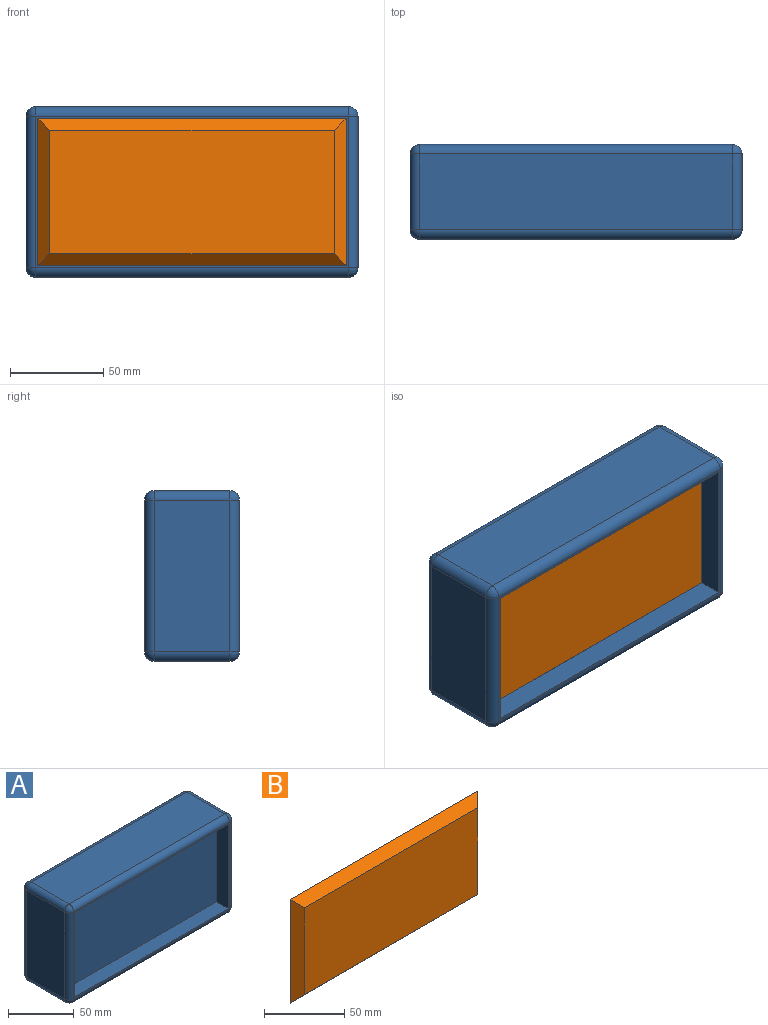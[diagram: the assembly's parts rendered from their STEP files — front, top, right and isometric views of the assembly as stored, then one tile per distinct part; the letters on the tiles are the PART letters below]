
ASSEMBLY  parts=2 mates=1
PART A: 31 faces, bbox 177.8x50.8x91.4 mm
  f0: plane 167.64x81.28mm, normal (0,-1,0), area 625.8mm2, adj f6,f7,f8,f9,f14,f15,f24,f25
  f1: plane 81.28x40.64mm, normal (1,0,0), area 3303.2mm2, adj f19,f24,f27,f30
  f2: plane 167.64x40.64mm, normal (0,0,1), area 6812.9mm2, adj f16,f25,f26,f30
  f3: plane 81.28x40.64mm, normal (-1,0,0), area 3303.2mm2, adj f11,f15,f16,f17
  f4: plane 167.64x40.64mm, normal (0,0,-1), area 6812.9mm2, adj f11,f14,f18,f19
  f5: plane 167.64x81.28mm, normal (0,1,0), area 13625.8mm2, adj f17,f18,f26,f27
  f6: plane 78.74x12.7mm, normal (1,0,0), area 1000mm2, adj f0,f7,f9,f10
  f7: plane 165.1x12.7mm, normal (0,0,1), area 2096.8mm2, adj f0,f6,f8,f10
  f8: plane 78.74x12.7mm, normal (-1,0,0), area 1000mm2, adj f0,f7,f9,f10
  f9: plane 165.1x12.7mm, normal (0,0,-1), area 2096.8mm2, adj f0,f6,f8,f10
  f10: plane 165.1x78.74mm, normal (0,-1,0), area 13000mm2, adj f6,f7,f8,f9
  f11: cylinder r=5.08mm len=40.64mm, axis (0,1,0), area 324.3mm2, adj f3,f4,f12,f13
  f12: sphere r=5.08mm, area 40.5mm2, adj f11,f14,f15
  f13: sphere r=5.08mm, area 40.5mm2, adj f11,f17,f18
  f14: cylinder r=5.08mm len=167.64mm, axis (-1,0,0), area 1337.7mm2, adj f0,f4,f12,f20
  f15: cylinder r=5.08mm len=81.28mm, axis (0,0,1), area 648.6mm2, adj f0,f3,f12,f21
  f16: cylinder r=5.08mm len=40.64mm, axis (0,-1,0), area 324.3mm2, adj f2,f3,f21,f22
  f17: cylinder r=5.08mm len=81.28mm, axis (0,0,-1), area 648.6mm2, adj f3,f5,f13,f22
  f18: cylinder r=5.08mm len=167.64mm, axis (1,0,0), area 1337.7mm2, adj f4,f5,f13,f23
  f19: cylinder r=5.08mm len=40.64mm, axis (0,-1,0), area 324.3mm2, adj f1,f4,f20,f23
  f20: sphere r=5.08mm, area 40.5mm2, adj f14,f19,f24
  f21: sphere r=5.08mm, area 40.5mm2, adj f15,f16,f25
  f22: sphere r=5.08mm, area 40.5mm2, adj f16,f17,f26
  f23: sphere r=5.08mm, area 40.5mm2, adj f18,f19,f27
  f24: cylinder r=5.08mm len=81.28mm, axis (0,0,-1), area 648.6mm2, adj f0,f1,f20,f28
  f25: cylinder r=5.08mm len=167.64mm, axis (1,0,0), area 1337.7mm2, adj f0,f2,f21,f28
  f26: cylinder r=5.08mm len=167.64mm, axis (-1,0,0), area 1337.7mm2, adj f2,f5,f22,f29
  f27: cylinder r=5.08mm len=81.28mm, axis (0,0,1), area 648.6mm2, adj f1,f5,f23,f29
  f28: sphere r=5.08mm, area 40.5mm2, adj f24,f25,f30
  f29: sphere r=5.08mm, area 40.5mm2, adj f26,f27,f30
  f30: cylinder r=5.08mm len=40.64mm, axis (0,1,0), area 324.3mm2, adj f1,f2,f28,f29
PART B: 6 faces, bbox 165.1x6.4x78.7 mm
  f0: plane 152.4x66.04mm, normal (0,-1,0), area 10064.5mm2, adj f2,f3,f4,f5
  f1: plane 165.1x78.74mm, normal (0,1,0), area 13000mm2, adj f2,f3,f4,f5
  f2: plane 78.74x6.35mm, normal (0.71,-0.71,0), area 650.1mm2, adj f0,f1,f3,f4
  f3: plane 165.1x6.35mm, normal (0,-0.71,-0.71), area 1425.6mm2, adj f0,f1,f2,f5
  f4: plane 165.1x6.35mm, normal (0,-0.71,0.71), area 1425.6mm2, adj f0,f1,f2,f5
  f5: plane 78.74x6.35mm, normal (-0.71,-0.71,0), area 650.1mm2, adj f0,f1,f3,f4
PLACE A t=(-77.86,-46.61,-64.39)mm
PLACE B t=(-77.86,-84.71,-64.39)mm
MATE fastened A.f10 <-> B.f1  axis (0,-1,0) through (-77.86,-84.71,-64.39)mm
